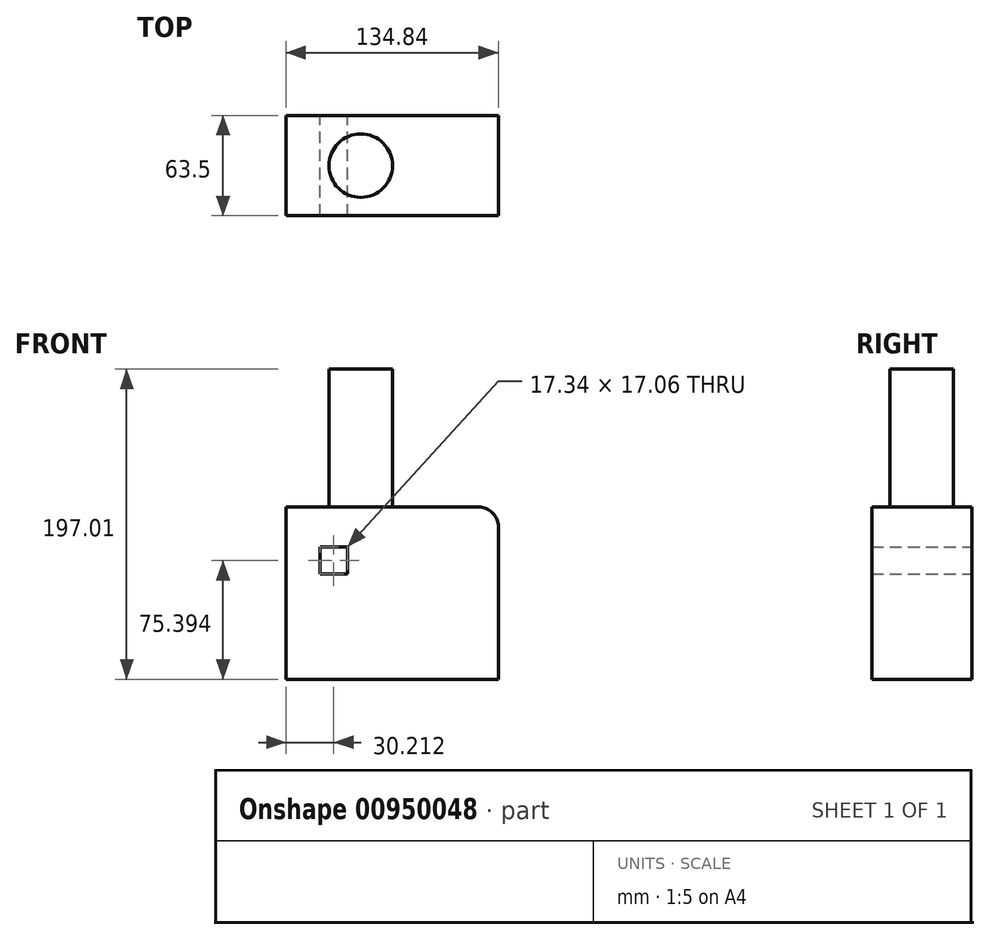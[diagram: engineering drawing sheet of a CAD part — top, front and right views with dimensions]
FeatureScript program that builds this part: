
annotation { "Feature Type Name" : "Feature", "Feature Type Description" : "" }
export const myFeature = defineFeature(function(context is Context, id is Id, definition is map)
    precondition{}
    {
        {
            var Q0;
            Q0=qCreatedBy(makeId("Front.planeOp"),FACE);
            var sketch = newSketch(context, id + "F0", { "sketchPlane" : qUnion([Q0])});
            skLineSegment(sketch, "E0.bottom", {"start": v(-67.8, 63.36) * mm, "end": v(67.04, 63.36) * mm});
            skLineSegment(sketch, "E0.top", {"start": v(-67.8, -46.02) * mm, "end": v(67.04, -46.02) * mm});
            skLineSegment(sketch, "E0.left", {"start": v(-67.8, 63.36) * mm, "end": v(-67.8, -46.02) * mm});
            skLineSegment(sketch, "E0.right", {"start": v(67.04, 63.36) * mm, "end": v(67.04, -46.02) * mm});
            skLineSegment(sketch, "E1.bottom", {"start": v(-46.26, 37.9) * mm, "end": v(-28.92, 37.9) * mm});
            skLineSegment(sketch, "E1.top", {"start": v(-46.26, 20.84) * mm, "end": v(-28.92, 20.84) * mm});
            skLineSegment(sketch, "E1.left", {"start": v(-46.26, 37.9) * mm, "end": v(-46.26, 20.84) * mm});
            skLineSegment(sketch, "E1.right", {"start": v(-28.92, 37.9) * mm, "end": v(-28.92, 20.84) * mm});
            skSolve(sketch);
        }
        {
            var Q0;
            Q0 = qSketchRegion(id + "F0", true);
            extrude(context, id + "F1", {"entities" : qUnion([Q0]), "depth" : 63.5 * mm, "offsetDistance" : 25.4 * mm});
        }
        {
            var Q0;
            Q0=makeQuery(id+"F1.opExtrude","SWEPT_EDGE",EDGE,{"disambiguationData":[OSD([sQuery(id+"F0.wireOp",EDGE,"E0.bottom"),sQuery(id+"F0.wireOp",EDGE,"E0.right")])]});
            fillet(context, id + "F2", {"entities" : qUnion([Q0]), "radius" : 12.7 * mm, "tangentPropagation" : true, "allowEdgeOverflow" : false});
        }
        {
            var Q0;
            Q0=makeQuery(id+"F1.opExtrude","SWEPT_FACE",FACE,{"disambiguationData":[OSD([sQuery(id+"F0.wireOp",EDGE,"E0.bottom")])]});
            var sketch = newSketch(context, id + "F3", { "sketchPlane" : qUnion([Q0])});
            skCircle(sketch, "E2", {"center": v(-20.38, -31.75) * mm, "radius": 20.17 * mm});
            skPoint(sketch, "E2.centerSnap0", {"position": v(-67.8, -31.75) * mm});
            skSolve(sketch);
        }
        {
            var Q0;
            Q0=makeQuery(id+"F3.imprint","IMPRINT",FACE,{"disambiguationData":[TD([[makeQuery(id+"F3.imprint","IMPRINT",EDGE,{"derivedFrom":sQuery(id+"F3.wireOp",EDGE,"E2")}),1.0]])]});
            extrude(context, id + "F4", {"entities" : qUnion([Q0]), "operationType" : NewBodyOperationType.ADD, "depth" : 87.63 * mm, "offsetDistance" : 25.4 * mm});
        }
    });
